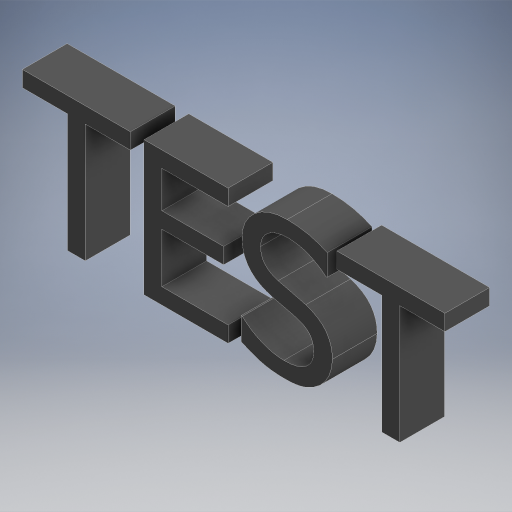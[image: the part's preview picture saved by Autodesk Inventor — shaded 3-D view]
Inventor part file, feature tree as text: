
AUTODESK INVENTOR PART (.ipt)
format: ipt  version: 2023 (Build 270158000, 158)  size: 321,536 bytes
history: native  units: in
note: dims shown in document units (in); Inventor stores cm internally (conversion verified against a paired STEP export)
features: extrude x1, sketch x1
ambient origin geometry x8: Origin, YZ Plane, XZ Plane, XY Plane, X Axis, Y Axis, Z Axis, Center Point
bodies: Solid1 (feature_tree)
feature tree (2):
  extrude  "Extrusion1"  [1 undecoded]
  sketch  "Sketch1"  dims[d0=1.0in d1=0.0in]
note: 1 required parameter value undecoded (feature->parameter linkage not recoverable at this tier; creation-order binding heuristic only, values carry confidence <= 0.55)
